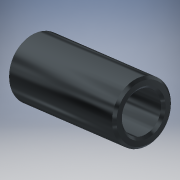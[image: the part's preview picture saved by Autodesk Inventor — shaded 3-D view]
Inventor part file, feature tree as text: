
AUTODESK INVENTOR PART (.ipt)
format: ipt  version: 2018 (Build 220112000, 112)  size: 114,688 bytes
history: native  units: mm
features: extrude x1, chamfer x1, sketch x1
ambient origin geometry x8: Origin, YZ Plane, XZ Plane, XY Plane, X Axis, Y Axis, Z Axis, Center Point
bodies: Solid1 (feature_tree)
feature tree (3):
  extrude  "Extrusion1"  Depth=2.0mm
  chamfer  "Chamfer1"  Distance=13.0mm
  sketch  "Sketch1"  dims[d0=6.0mm d1=4.0mm d2=13.0mm d3=0.0mm d4=0.25mm d5=2.0mm d6=45.0deg]
